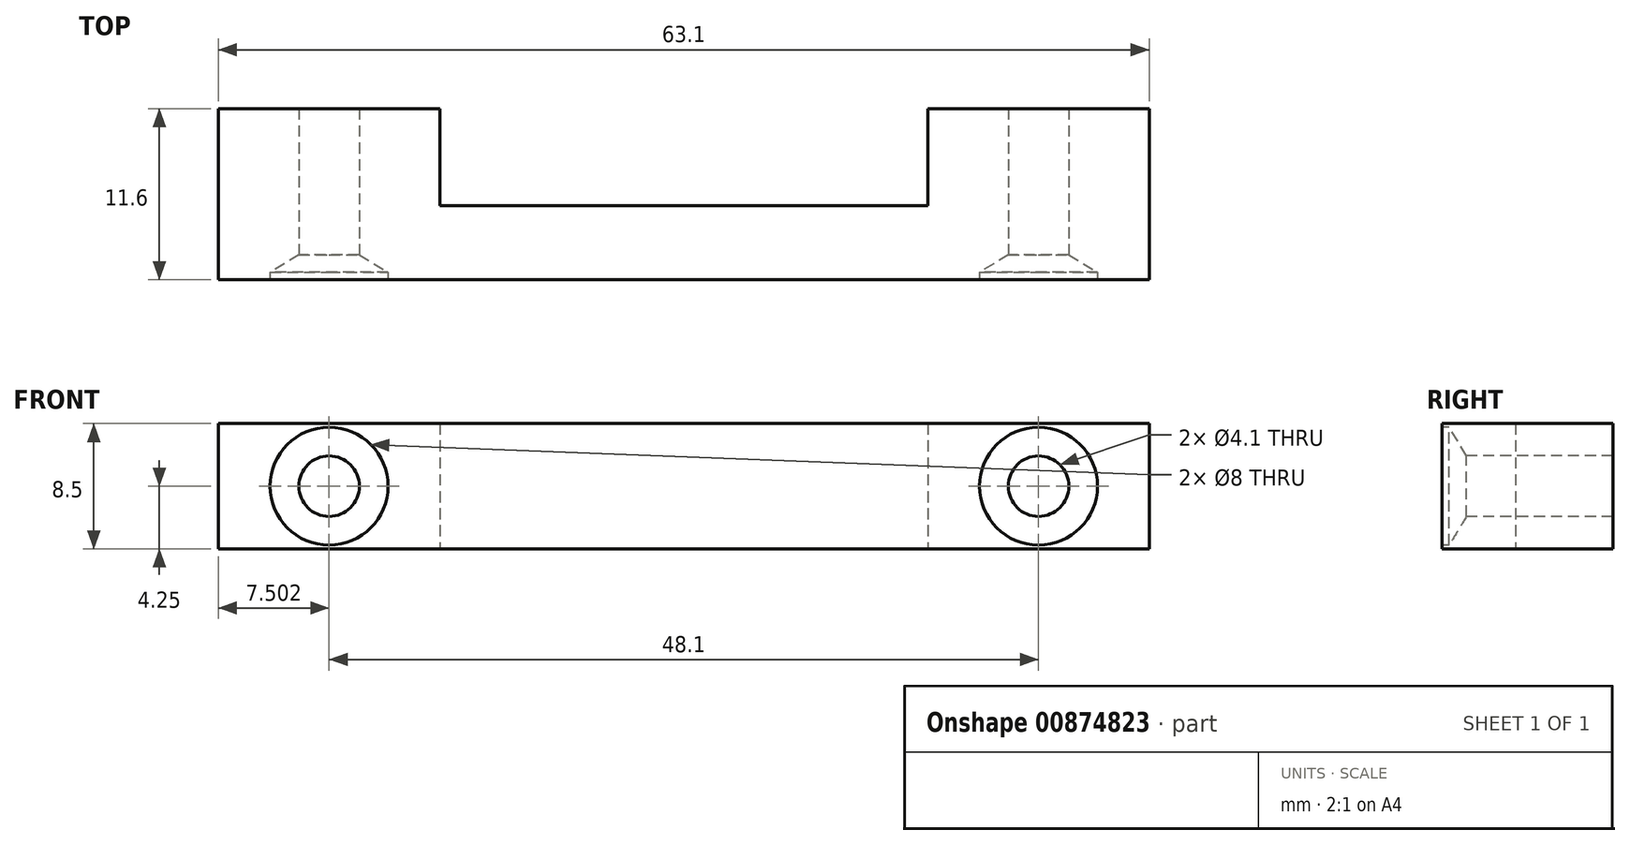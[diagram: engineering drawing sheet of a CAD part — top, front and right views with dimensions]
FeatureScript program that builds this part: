
annotation { "Feature Type Name" : "Feature", "Feature Type Description" : "" }
export const myFeature = defineFeature(function(context is Context, id is Id, definition is map)
    precondition{}
    {
        {
            var Q0;
            Q0=qCreatedBy(makeId("Top.planeOp"),FACE);
            var sketch = newSketch(context, id + "F0", { "sketchPlane" : qUnion([Q0])});
            skLineSegment(sketch, "E0.top", {"start": v(-21.85, 0.51) * mm, "end": v(41.25, 0.51) * mm});
            skLineSegment(sketch, "E0.left", {"start": v(-21.85, 5.51) * mm, "end": v(-21.85, 0.51) * mm});
            skLineSegment(sketch, "E0.right", {"start": v(41.25, 5.51) * mm, "end": v(41.25, 0.51) * mm});
            skPoint(sketch, "E1", {"position": v(-6.85, 5.51) * mm});
            skPoint(sketch, "E2", {"position": v(26.25, 5.51) * mm});
            skLineSegment(sketch, "E3.top", {"start": v(-6.85, 12.11) * mm, "end": v(-21.85, 12.11) * mm});
            skLineSegment(sketch, "E3.left", {"start": v(-6.85, 5.51) * mm, "end": v(-6.85, 12.11) * mm});
            skLineSegment(sketch, "E3.right", {"start": v(-21.85, 5.51) * mm, "end": v(-21.85, 12.11) * mm});
            skLineSegment(sketch, "E4.top", {"start": v(26.25, 12.11) * mm, "end": v(41.25, 12.11) * mm});
            skLineSegment(sketch, "E4.left", {"start": v(26.25, 5.51) * mm, "end": v(26.25, 12.11) * mm});
            skLineSegment(sketch, "E4.right", {"start": v(41.25, 5.51) * mm, "end": v(41.25, 12.11) * mm});
            skLineSegment(sketch, "E5", {"start": v(-6.85, 5.51) * mm, "end": v(26.25, 5.51) * mm});
            skSolve(sketch);
        }
        {
            var Q0;
            Q0=makeQuery(id+"F0.imprint","IMPRINT",FACE,{"disambiguationData":[TD([[makeQuery(id+"F0.imprint","IMPRINT",EDGE,{"derivedFrom":sQuery(id+"F0.wireOp",EDGE,"E0.top")}),1.0]])]});
            extrude(context, id + "F1", {"entities" : qUnion([Q0]), "depth" : 8.5 * mm, "offsetDistance" : 25 * mm});
        }
        {
            var Q0;
            Q0=makeQuery(id+"F1.opExtrude","SWEPT_FACE",FACE,{"disambiguationData":[OSD([sQuery(id+"F0.wireOp",EDGE,"E0.top")])]});
            var sketch = newSketch(context, id + "F2", { "sketchPlane" : qUnion([Q0])});
            skLineSegment(sketch, "E6.bottom", {"start": v(-21.85, 0) * mm, "end": v(-6.85, 0) * mm});
            skLineSegment(sketch, "E6.top", {"start": v(-21.85, 8.5) * mm, "end": v(-6.85, 8.5) * mm});
            skLineSegment(sketch, "E6.left", {"start": v(-21.85, 0) * mm, "end": v(-21.85, 8.5) * mm});
            skLineSegment(sketch, "E6.right", {"start": v(-6.85, 0) * mm, "end": v(-6.85, 8.5) * mm});
            skLineSegment(sketch, "E7.bottom", {"start": v(41.25, 0) * mm, "end": v(26.25, 0) * mm});
            skLineSegment(sketch, "E7.top", {"start": v(41.25, 8.5) * mm, "end": v(26.25, 8.5) * mm});
            skLineSegment(sketch, "E7.left", {"start": v(41.25, 0) * mm, "end": v(41.25, 8.5) * mm});
            skLineSegment(sketch, "E7.right", {"start": v(26.25, 0) * mm, "end": v(26.25, 8.5) * mm});
            skPoint(sketch, "E8", {"position": v(-14.35, 4.25) * mm});
            skPoint(sketch, "E8.positionSnap0", {"position": v(-21.85, 4.25) * mm});
            skPoint(sketch, "E8.positionSnap1", {"position": v(-14.35, 8.5) * mm});
            skPoint(sketch, "E9", {"position": v(33.75, 4.25) * mm});
            skPoint(sketch, "E9.positionSnap0", {"position": v(33.75, 8.5) * mm});
            skPoint(sketch, "E9.positionSnap1", {"position": v(41.25, 4.25) * mm});
            skCircle(sketch, "E10", {"center": v(-14.35, 4.25) * mm, "radius": 3 * mm});
            skCircle(sketch, "E11", {"center": v(-14.35, 4.25) * mm, "radius": 2.5 * mm});
            skCircle(sketch, "E12", {"center": v(33.75, 4.25) * mm, "radius": 3 * mm});
            skCircle(sketch, "E13", {"center": v(33.75, 4.25) * mm, "radius": 2.5 * mm});
            skSolve(sketch);
        }
        {
            var Q0;
            Q0=sQuery(id+"F2.wireOp",VERTEX,"E8");
            var Q1;
            Q1=sQuery(id+"F2.wireOp",VERTEX,"E9");
            var Q2;
            Q2=makeQuery(id+"F1.opExtrude","SWEPT_BODY",BODY,{"disambiguationData":[OSD([sQuery(id+"F0.wireOp",EDGE,"E0.top"),sQuery(id+"F0.wireOp",EDGE,"E0.left"),sQuery(id+"F0.wireOp",EDGE,"E0.right"),sQuery(id+"F0.wireOp",EDGE,"E3.top"),sQuery(id+"F0.wireOp",EDGE,"E3.left"),sQuery(id+"F0.wireOp",EDGE,"E3.right"),sQuery(id+"F0.wireOp",EDGE,"E4.top"),sQuery(id+"F0.wireOp",EDGE,"E4.left"),sQuery(id+"F0.wireOp",EDGE,"E4.right"),sQuery(id+"F0.wireOp",EDGE,"E5")])]});
            hole(context, id + "F3", {"style" : HoleStyle.SIMPLE, "endStyle" : HoleEndStyle.BLIND, "holeDiameter" : 4.1 * mm, "majorDiameter" : 5 * mm, "holeDepth" : 12 * mm, "isTappedThrough" : true, "tappedDepth" : 12 * mm, "tapClearance" : 3, "locations" : qUnion([Q0, Q1]), "scope" : qUnion([Q2])});
        }
        {
            var Q0;
            Q0=sQuery(id+"F2.wireOp",VERTEX,"E8");
            var Q1;
            Q1=sQuery(id+"F2.wireOp",VERTEX,"E9");
            var Q2;
            Q2=makeQuery(id+"F1.opExtrude","SWEPT_BODY",BODY,{"disambiguationData":[OSD([sQuery(id+"F0.wireOp",EDGE,"E0.top"),sQuery(id+"F0.wireOp",EDGE,"E0.left"),sQuery(id+"F0.wireOp",EDGE,"E0.right"),sQuery(id+"F0.wireOp",EDGE,"E3.top"),sQuery(id+"F0.wireOp",EDGE,"E3.left"),sQuery(id+"F0.wireOp",EDGE,"E3.right"),sQuery(id+"F0.wireOp",EDGE,"E4.top"),sQuery(id+"F0.wireOp",EDGE,"E4.left"),sQuery(id+"F0.wireOp",EDGE,"E4.right"),sQuery(id+"F0.wireOp",EDGE,"E5")])]});
            hole(context, id + "F4", {"style" : HoleStyle.SIMPLE, "endStyle" : HoleEndStyle.BLIND, "holeDiameter" : 8 * mm, "majorDiameter" : 5 * mm, "holeDepth" : .5 * mm, "isTappedThrough" : true, "tappedDepth" : 12 * mm, "tapClearance" : 3, "locations" : qUnion([Q0, Q1]), "scope" : qUnion([Q2])});
        }
    });
